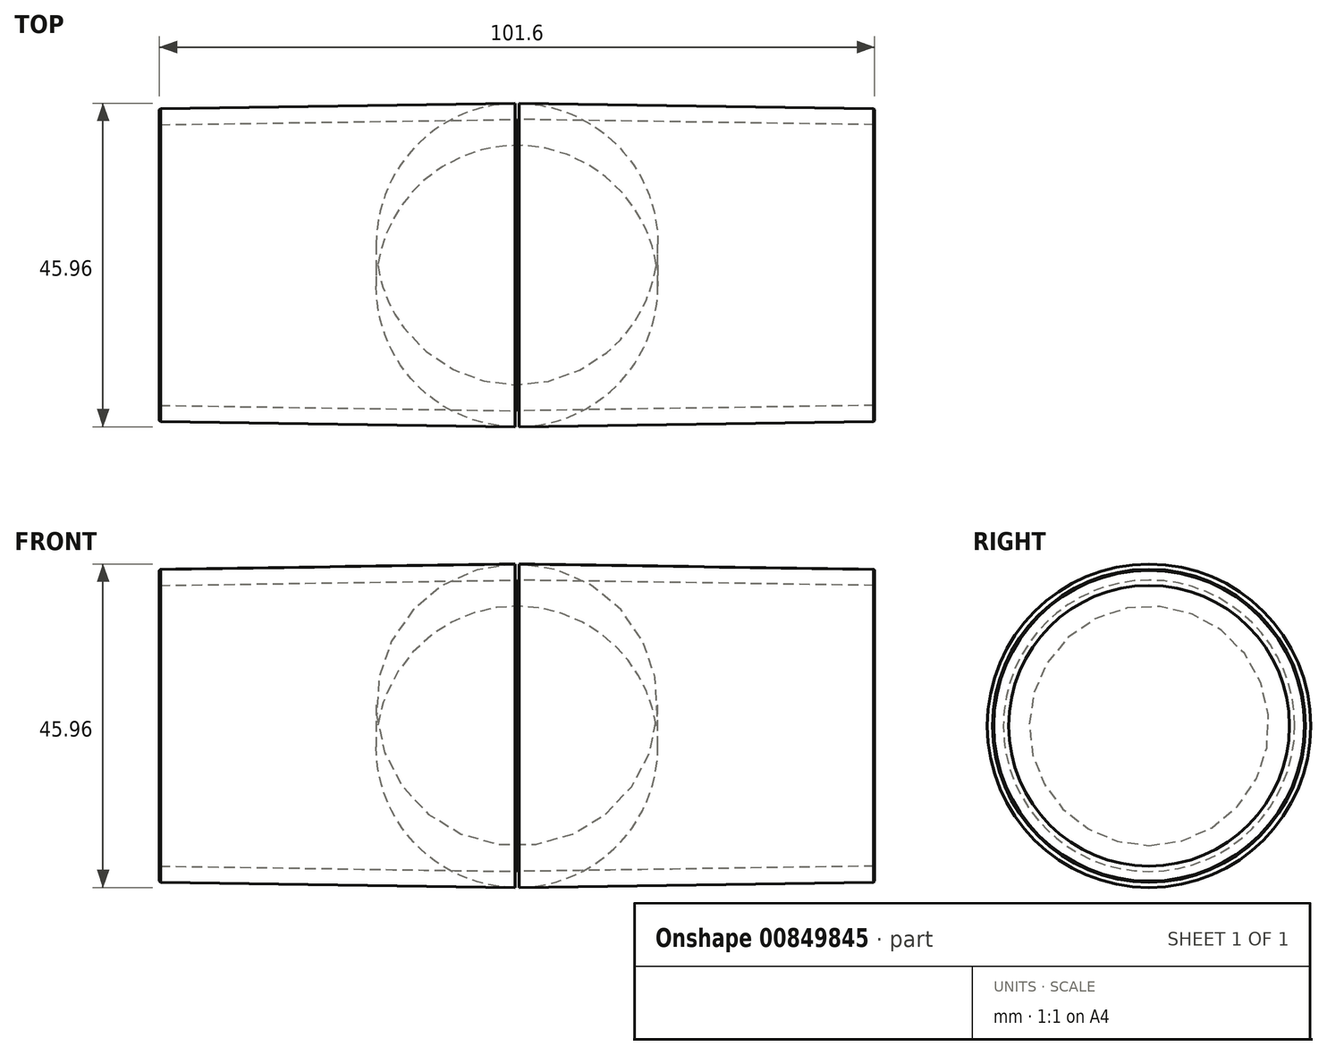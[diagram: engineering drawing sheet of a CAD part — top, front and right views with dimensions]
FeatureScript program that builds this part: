
annotation { "Feature Type Name" : "Feature", "Feature Type Description" : "" }
export const myFeature = defineFeature(function(context is Context, id is Id, definition is map)
    precondition{}
    {
        {
            assignVariable(context, id + "F0", {"name" : "OD_radius", "anyValue" : 20});
        }
        {
            assignVariable(context, id + "F1", {"name" : "chamfer", "anyValue" : .15});
        }
        {
            var Q0;
            Q0=qCreatedBy(makeId("Front.planeOp"),FACE);
            var sketch = newSketch(context, id + "F2", { "sketchPlane" : qUnion([Q0])});
            skLineSegment(sketch, "E0", {"start": v(0, 22.99) * mm, "end": v(50.8, 22.23) * mm});
            skLineSegment(sketch, "E1", {"start": v(0, 0) * mm, "end": v(-86.25, 0) * mm, "construction": true});
            skPoint(sketch, "E2", {"position": v(25.4, 22.6) * mm});
            skLineSegment(sketch, "E3", {"start": v(0, 22.99) * mm, "end": v(0, 20.7) * mm});
            skLineSegment(sketch, "E4", {"start": v(0, 20.7) * mm, "end": v(50.8, 19.94) * mm});
            skLineSegment(sketch, "E5", {"start": v(50.8, 19.94) * mm, "end": v(50.8, 22.23) * mm});
            skSolve(sketch);
        }
        {
            var Q0;
            Q0=qSketchRegion(id+"F2",true);
            var Q1;
            Q1=sQuery(id+"F2.wireOp",EDGE,"E1");
            revolve(context, id + "F3", {"surfaceOperationType" : NewSurfaceOperationType.NEW, "entities" : qUnion([Q0]), "axis" : qUnion([Q1]), "revolveType" : RevolveType.FULL});
        }
        {
            var Q0;
            Q0=makeQuery(id+"F3.opRevolve","SWEPT_BODY",BODY,{"disambiguationData":[OSD([sQuery(id+"F2.wireOp",EDGE,"E0"),sQuery(id+"F2.wireOp",EDGE,"E3"),sQuery(id+"F2.wireOp",EDGE,"E4"),sQuery(id+"F2.wireOp",EDGE,"E5")])]});
            var Q1;
            Q1=makeQuery(id+"F3.opRevolve","SWEPT_FACE",FACE,{"disambiguationData":[OSD([sQuery(id+"F2.wireOp",EDGE,"E3")])]});
            mirror(context, id + "F4", {"operationType" : NewBodyOperationType.ADD, "entities" : qUnion([Q0]), "mirrorPlane" : qUnion([Q1])});
        }
        {
            var Q0;
            {var subQ0=makeQuery(id+"F3.opRevolve","SWEPT_EDGE",EDGE,{"disambiguationData":[OSD([sQuery(id+"F2.wireOp",EDGE,"E0"),sQuery(id+"F2.wireOp",EDGE,"E3")])]});Q0=makeQuery(id+"F4.boolean.opBoolean","MERGE",EDGE,{"derivedFrom":[subQ0,makeQuery(id+"F4.opPattern","COPY",EDGE,{"derivedFrom":subQ0,"instanceName":"1"})]});}
            fillet(context, id + "F5", {"entities" : qUnion([Q0]), "radius" : (getVariable(context, 'OD_radius')) * mm, "tangentPropagation" : true, "allowEdgeOverflow" : false});
        }
        {
            var Q0;
            Q0=makeQuery(id+"F4.opPattern","COPY",EDGE,{"derivedFrom":makeQuery(id+"F3.opRevolve","SWEPT_EDGE",EDGE,{"disambiguationData":[OSD([sQuery(id+"F2.wireOp",EDGE,"E0"),sQuery(id+"F2.wireOp",EDGE,"E5")])]}),"instanceName":"1"});
            var Q1;
            Q1=makeQuery(id+"F3.opRevolve","SWEPT_EDGE",EDGE,{"disambiguationData":[OSD([sQuery(id+"F2.wireOp",EDGE,"E0"),sQuery(id+"F2.wireOp",EDGE,"E5")])]});
            chamfer(context, id + "F6", {"entities" : qUnion([Q0, Q1]), "width" : (getVariable(context, 'chamfer')) * mm, "tangentPropagation" : true});
        }
    });
